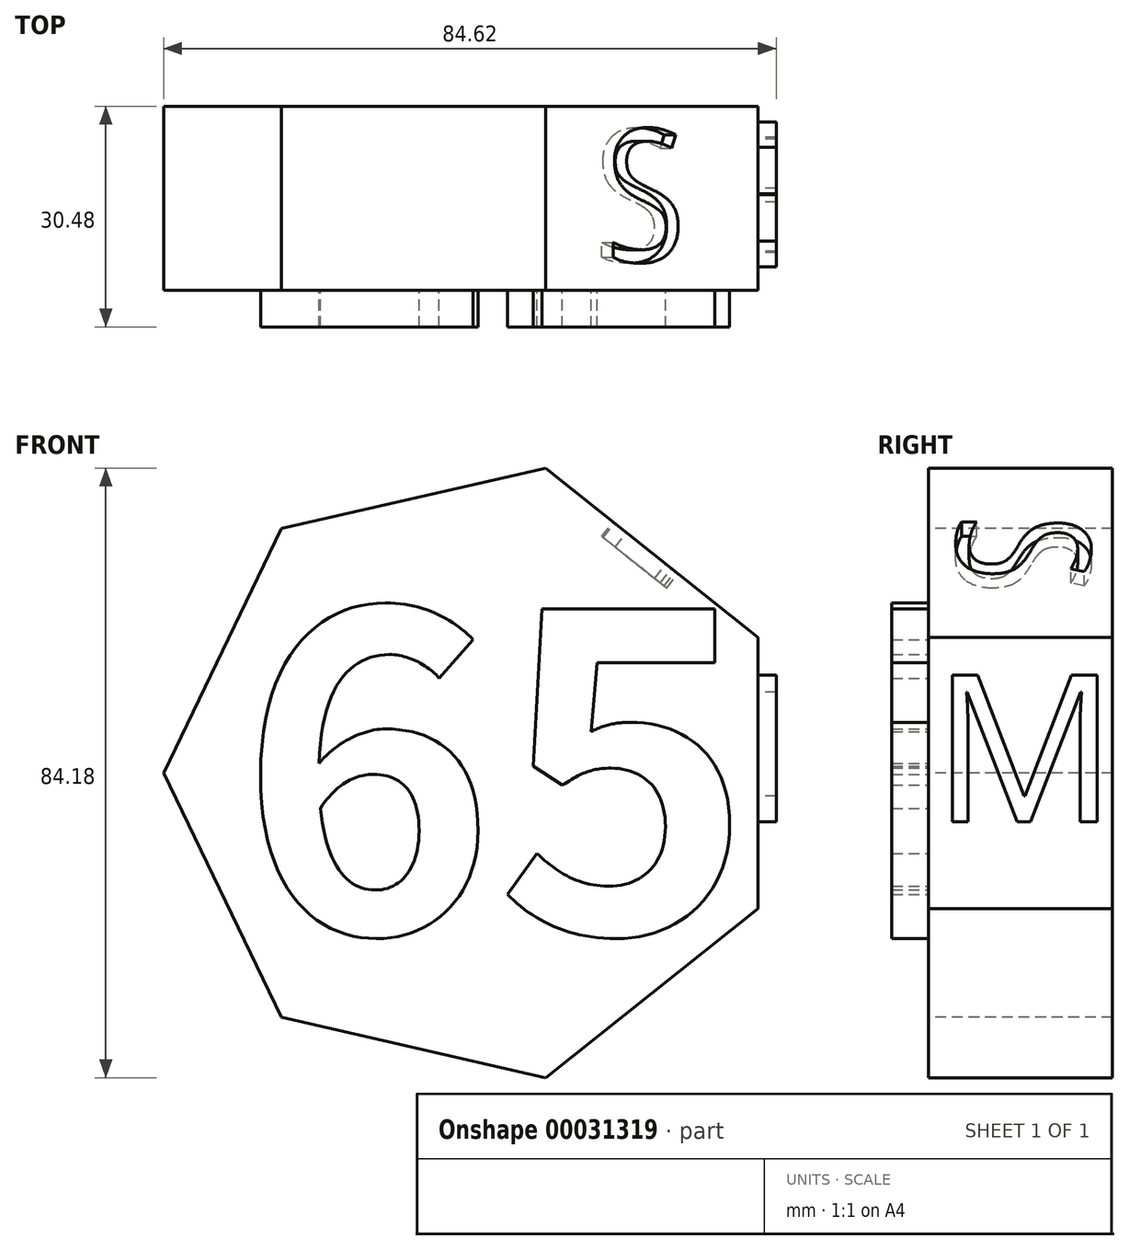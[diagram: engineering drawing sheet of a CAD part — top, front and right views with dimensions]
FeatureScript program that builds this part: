
annotation { "Feature Type Name" : "Feature", "Feature Type Description" : "" }
export const myFeature = defineFeature(function(context is Context, id is Id, definition is map)
    precondition{}
    {
        {
            var Q0;
            Q0=qCreatedBy(makeId("Front.planeOp"),FACE);
            var sketch = newSketch(context, id + "F0", { "sketchPlane" : qUnion([Q0])});
            skCircle(sketch, "E0.cCircle", {"center": v(0, 0) * mm, "radius": 43.18 * mm, "construction": true});
            skLineSegment(sketch, "E0.0", {"start": v(9.6, 42.1) * mm, "end": v(38.9, 18.73) * mm});
            skLineSegment(sketch, "E0.1", {"start": v(38.9, 18.73) * mm, "end": v(38.9, -18.73) * mm});
            skLineSegment(sketch, "E0.2", {"start": v(38.9, -18.73) * mm, "end": v(9.6, -42.1) * mm});
            skLineSegment(sketch, "E0.3", {"start": v(9.6, -42.1) * mm, "end": v(-26.92, -33.76) * mm});
            skLineSegment(sketch, "E0.4", {"start": v(-26.92, -33.76) * mm, "end": v(-43.18, 0) * mm});
            skLineSegment(sketch, "E0.5", {"start": v(-43.18, 0) * mm, "end": v(-26.92, 33.76) * mm});
            skLineSegment(sketch, "E0.6", {"start": v(-26.92, 33.76) * mm, "end": v(9.6, 42.1) * mm});
            skSolve(sketch);
        }
        {
            var Q0;
            Q0=makeQuery(id+"F0.imprint","IMPRINT",FACE,{"disambiguationData":[TD([[makeQuery(id+"F0.imprint","IMPRINT",EDGE,{"derivedFrom":sQuery(id+"F0.wireOp",EDGE,"E0.0")}),-1.0]])]});
            extrude(context, id + "F1", {"entities" : qUnion([Q0]), "oppositeDirection" : true, "depth" : 25.4 * mm});
        }
        {
            var Q0;
            Q0=makeQuery(id+"F1.opExtrude","SWEPT_FACE",FACE,{"disambiguationData":[OSD([sQuery(id+"F0.wireOp",EDGE,"E0.0")])]});
            var sketch = newSketch(context, id + "F2", { "sketchPlane" : qUnion([Q0])});
            skText(sketch, "E1", { "text": "S", "fontName": "OpenSans-Regular.ttf"});
            const initialGuessF2  = {"E1": [-0.00814, 0.00398, 1, 0, 0.01839]};
            skSetInitialGuess(sketch, initialGuessF2);
            skSolve(sketch);
        }
        {
            var Q0;
            Q0 = qSketchRegion(id + "F2", true);
            extrude(context, id + "F3", {"entities" : qUnion([Q0]), "operationType" : NewBodyOperationType.REMOVE, "oppositeDirection" : true, "depth" : 2.54 * mm});
        }
        {
            var Q0;
            Q0=makeQuery(id+"F1.opExtrude","SWEPT_FACE",FACE,{"disambiguationData":[OSD([sQuery(id+"F0.wireOp",EDGE,"E0.1")])]});
            var sketch = newSketch(context, id + "F4", { "sketchPlane" : qUnion([Q0])});
            skText(sketch, "E2", { "text": "M", "fontName": "OpenSans-Regular.ttf"});
            const initialGuessF4  = {"E2": [0.00047, -0.00672, 1, 0, 0.02038]};
            skSetInitialGuess(sketch, initialGuessF4);
            skSolve(sketch);
        }
        {
            var Q0;
            Q0 = qSketchRegion(id + "F4", true);
            extrude(context, id + "F5", {"entities" : qUnion([Q0]), "operationType" : NewBodyOperationType.ADD, "depth" : 2.54 * mm});
        }
        {
            var Q0;
            Q0=makeQuery(id+"F1.opExtrude","CAP_FACE",FACE,{"disambiguationData":[OSD([sQuery(id+"F0.wireOp",EDGE,"E0.0"),sQuery(id+"F0.wireOp",EDGE,"E0.1"),sQuery(id+"F0.wireOp",EDGE,"E0.2"),sQuery(id+"F0.wireOp",EDGE,"E0.3"),sQuery(id+"F0.wireOp",EDGE,"E0.4"),sQuery(id+"F0.wireOp",EDGE,"E0.5"),sQuery(id+"F0.wireOp",EDGE,"E0.6")])],"isStart":true});
            var sketch = newSketch(context, id + "F6", { "sketchPlane" : qUnion([Q0])});
            skText(sketch, "E3", { "text": "65", "fontName": "NotoSansCJKkr-Bold.otf"});
            const initialGuessF6  = {"E3": [-0.03282, -0.02203, 1, 0, 0.04345]};
            skSetInitialGuess(sketch, initialGuessF6);
            skSolve(sketch);
        }
        {
            var Q0;
            Q0 = qSketchRegion(id + "F6", true);
            extrude(context, id + "F7", {"entities" : qUnion([Q0]), "operationType" : NewBodyOperationType.ADD, "depth" : 5.08 * mm});
        }
    });
